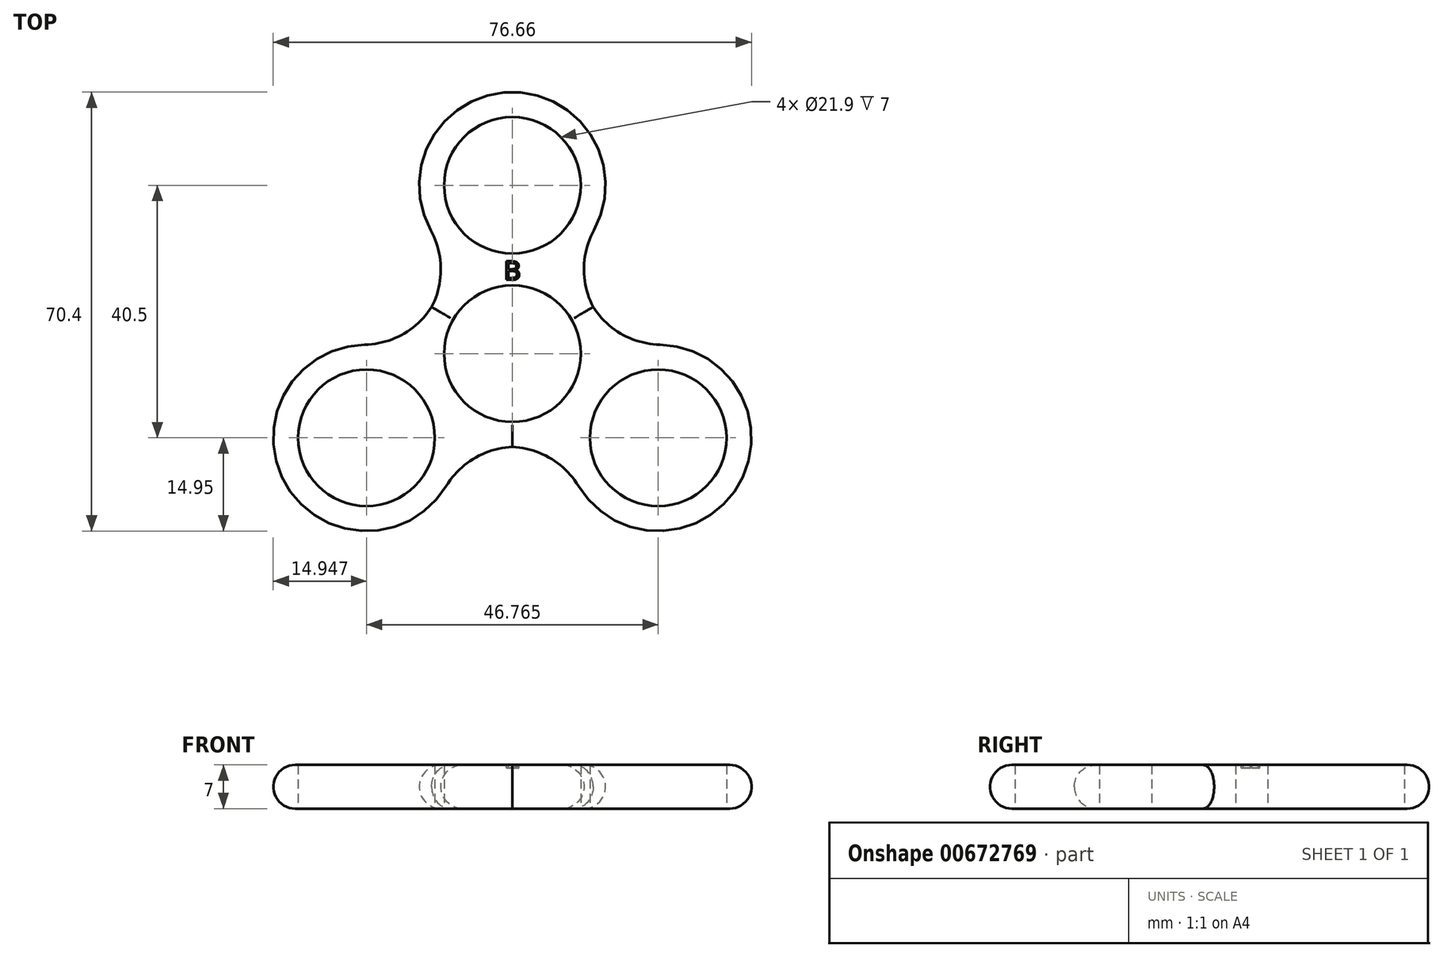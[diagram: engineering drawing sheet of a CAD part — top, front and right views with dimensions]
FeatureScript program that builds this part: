
annotation { "Feature Type Name" : "Feature", "Feature Type Description" : "" }
export const myFeature = defineFeature(function(context is Context, id is Id, definition is map)
    precondition{}
    {
        {
            var Q0;
            Q0=qCreatedBy(makeId("Top.planeOp"),FACE);
            var sketch = newSketch(context, id + "F0", { "sketchPlane" : qUnion([Q0])});
            skCircle(sketch, "E0", {"center": v(0, 0) * mm, "radius": 10.95 * mm});
            skCircle(sketch, "E1.cCircle", {"center": v(0, 0) * mm, "radius": 13.5 * mm, "construction": true});
            skLineSegment(sketch, "E1.0", {"start": v(-23.38, -13.5) * mm, "end": v(0, 27) * mm, "construction": true});
            skLineSegment(sketch, "E1.1", {"start": v(0, 27) * mm, "end": v(23.38, -13.5) * mm, "construction": true});
            skLineSegment(sketch, "E1.2", {"start": v(23.38, -13.5) * mm, "end": v(-23.38, -13.5) * mm, "construction": true});
            skPoint(sketch, "E1.0.midPoint", {"position": v(-11.7, 6.75) * mm});
            skCircle(sketch, "E2", {"center": v(0, 27) * mm, "radius": 10.95 * mm});
            skCircle(sketch, "E3", {"center": v(23.38, -13.5) * mm, "radius": 10.95 * mm});
            skCircle(sketch, "E4", {"center": v(-23.38, -13.5) * mm, "radius": 10.95 * mm});
            skCircle(sketch, "E5.0", {"center": v(-23.38, -13.5) * mm, "radius": 14.95 * mm});
            skCircle(sketch, "E6.0", {"center": v(23.38, -13.5) * mm, "radius": 14.95 * mm});
            skCircle(sketch, "E7.0", {"center": v(0, 27) * mm, "radius": 14.95 * mm});
            skCircle(sketch, "E8.0", {"center": v(0, 0) * mm, "radius": 14.95 * mm});
            skSolve(sketch);
        }
        {
            var Q0;
            Q0=qSketchRegion(id+"F0",true);
            extrude(context, id + "F1", {"entities" : qUnion([Q0]), "depth" : 7 * mm, "offsetDistance" : 25 * mm});
        }
        {
            var Q0;
            {var subQ0=sQuery(id+"F0.wireOp",EDGE,"E8.0");var subQ1=sQuery(id+"F0.wireOp",EDGE,"E5.0");Q0=makeQuery(id+"F1.opExtrude","SWEPT_EDGE",EDGE,{"disambiguationData":[OSD([subQ1,subQ0]),TDD([makeQuery(id+"F0.imprint","INTERSECT",VERTEX,{"disambiguationData":[OD(1.0)],"derivedFrom":[subQ1,subQ0]})])]});}
            var Q1;
            {var subQ0=sQuery(id+"F0.wireOp",EDGE,"E8.0");var subQ1=sQuery(id+"F0.wireOp",EDGE,"E6.0");Q1=makeQuery(id+"F1.opExtrude","SWEPT_EDGE",EDGE,{"disambiguationData":[OSD([subQ1,subQ0]),TDD([makeQuery(id+"F0.imprint","INTERSECT",VERTEX,{"disambiguationData":[OD(0.0)],"derivedFrom":[subQ1,subQ0]})])]});}
            var Q2;
            {var subQ0=sQuery(id+"F0.wireOp",EDGE,"E8.0");var subQ1=sQuery(id+"F0.wireOp",EDGE,"E7.0");Q2=makeQuery(id+"F1.opExtrude","SWEPT_EDGE",EDGE,{"disambiguationData":[OSD([subQ1,subQ0]),TDD([makeQuery(id+"F0.imprint","INTERSECT",VERTEX,{"disambiguationData":[OD(1.0)],"derivedFrom":[subQ1,subQ0]})])]});}
            var Q3;
            {var subQ0=sQuery(id+"F0.wireOp",EDGE,"E8.0");var subQ1=sQuery(id+"F0.wireOp",EDGE,"E6.0");Q3=makeQuery(id+"F1.opExtrude","SWEPT_EDGE",EDGE,{"disambiguationData":[OSD([subQ1,subQ0]),TDD([makeQuery(id+"F0.imprint","INTERSECT",VERTEX,{"disambiguationData":[OD(1.0)],"derivedFrom":[subQ1,subQ0]})])]});}
            var Q4;
            {var subQ0=sQuery(id+"F0.wireOp",EDGE,"E8.0");var subQ1=sQuery(id+"F0.wireOp",EDGE,"E7.0");Q4=makeQuery(id+"F1.opExtrude","SWEPT_EDGE",EDGE,{"disambiguationData":[OSD([subQ1,subQ0]),TDD([makeQuery(id+"F0.imprint","INTERSECT",VERTEX,{"disambiguationData":[OD(0.0)],"derivedFrom":[subQ1,subQ0]})])]});}
            var Q5;
            {var subQ0=sQuery(id+"F0.wireOp",EDGE,"E8.0");var subQ1=sQuery(id+"F0.wireOp",EDGE,"E5.0");Q5=makeQuery(id+"F1.opExtrude","SWEPT_EDGE",EDGE,{"disambiguationData":[OSD([subQ1,subQ0]),TDD([makeQuery(id+"F0.imprint","INTERSECT",VERTEX,{"disambiguationData":[OD(0.0)],"derivedFrom":[subQ1,subQ0]})])]});}
            fillet(context, id + "F2", {"entities" : qUnion([Q0, Q1, Q2, Q3, Q4, Q5]), "radius" : 13 * mm, "tangentPropagation" : true, "allowEdgeOverflow" : false});
        }
        {
            var Q0;
            Q0=makeQuery(id+"F1.opExtrude","CAP_EDGE",EDGE,{"disambiguationData":[OSD([sQuery(id+"F0.wireOp",EDGE,"E7.0")])],"isStart":false});
            var Q1;
            Q1=makeQuery(id+"F1.opExtrude","CAP_EDGE",EDGE,{"disambiguationData":[OSD([sQuery(id+"F0.wireOp",EDGE,"E7.0")])],"isStart":true});
            var Q2;
            Q2=makeQuery(id+"F1.opExtrude","CAP_EDGE",EDGE,{"disambiguationData":[OSD([sQuery(id+"F0.wireOp",EDGE,"E5.0")])],"isStart":false});
            var Q3;
            Q3=makeQuery(id+"F1.opExtrude","CAP_EDGE",EDGE,{"disambiguationData":[OSD([sQuery(id+"F0.wireOp",EDGE,"E5.0")])],"isStart":true});
            var Q4;
            Q4=makeQuery(id+"F1.opExtrude","CAP_EDGE",EDGE,{"disambiguationData":[OSD([sQuery(id+"F0.wireOp",EDGE,"E6.0")])],"isStart":false});
            var Q5;
            Q5=makeQuery(id+"F1.opExtrude","CAP_EDGE",EDGE,{"disambiguationData":[OSD([sQuery(id+"F0.wireOp",EDGE,"E6.0")])],"isStart":true});
            fillet(context, id + "F3", {"entities" : qUnion([Q0, Q1, Q2, Q3, Q4, Q5]), "radius" : 3.5 * mm, "tangentPropagation" : true, "allowEdgeOverflow" : false});
        }
        {
            var Q0;
            Q0=makeQuery(id+"F1.opExtrude","CAP_FACE",FACE,{"disambiguationData":[OSD([sQuery(id+"F0.wireOp",EDGE,"E0"),sQuery(id+"F0.wireOp",EDGE,"E2"),sQuery(id+"F0.wireOp",EDGE,"E3"),sQuery(id+"F0.wireOp",EDGE,"E4"),sQuery(id+"F0.wireOp",EDGE,"E5.0"),sQuery(id+"F0.wireOp",EDGE,"E6.0"),sQuery(id+"F0.wireOp",EDGE,"E7.0"),sQuery(id+"F0.wireOp",EDGE,"E8.0")])],"isStart":false});
            var sketch = newSketch(context, id + "F4", { "sketchPlane" : qUnion([Q0])});
            skText(sketch, "E9", { "text": "B", "fontName": "OpenSans-Regular.ttf"});
            const initialGuessF4  = {"E9": [-0.00137, 0.01184, 1, 0, 0.003]};
            skSetInitialGuess(sketch, initialGuessF4);
            skSolve(sketch);
        }
        {
            var Q0;
            Q0 = qSketchRegion(id + "F4", true);
            extrude(context, id + "F5", {"entities" : qUnion([Q0]), "operationType" : NewBodyOperationType.REMOVE, "oppositeDirection" : true, "depth" : .5 * mm, "offsetDistance" : 25 * mm});
        }
    });
